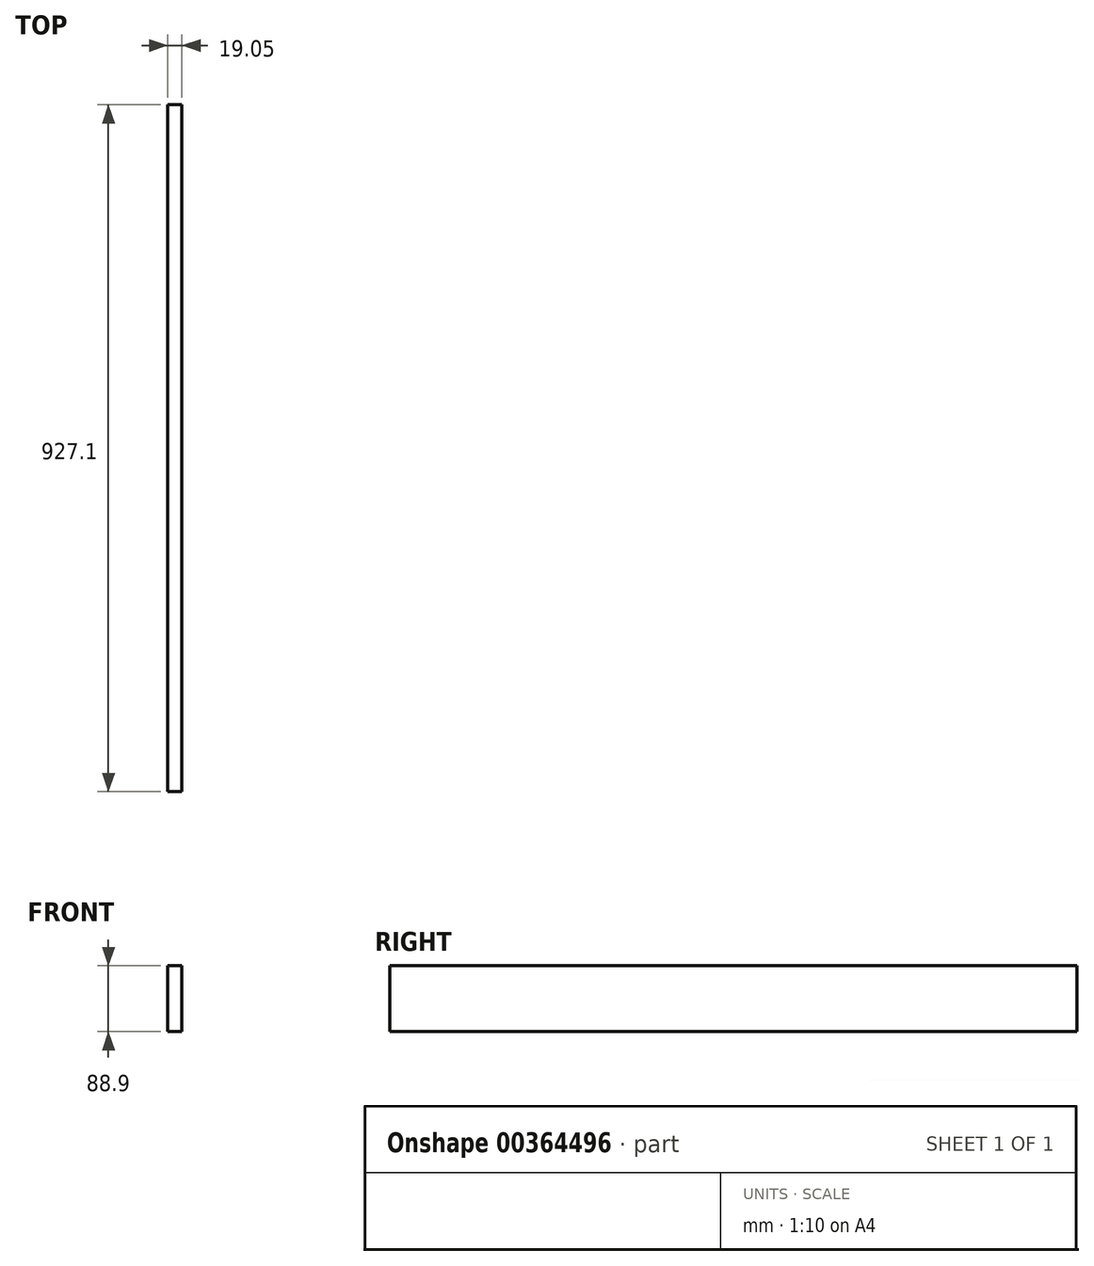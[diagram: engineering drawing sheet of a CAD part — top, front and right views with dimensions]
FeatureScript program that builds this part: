
annotation { "Feature Type Name" : "Feature", "Feature Type Description" : "" }
export const myFeature = defineFeature(function(context is Context, id is Id, definition is map)
    precondition{}
    {
        {
            var Q0;
            Q0=qCreatedBy(makeId("Right.planeOp"),FACE);
            var sketch = newSketch(context, id + "F0", { "sketchPlane" : qUnion([Q0])});
            skLineSegment(sketch, "E0.bottom", {"start": v(0, 0) * mm, "end": v(927.1, 0) * mm});
            skLineSegment(sketch, "E0.top", {"start": v(0, 88.9) * mm, "end": v(927.1, 88.9) * mm});
            skLineSegment(sketch, "E0.left", {"start": v(0, 0) * mm, "end": v(0, 88.9) * mm});
            skLineSegment(sketch, "E0.right", {"start": v(927.1, 0) * mm, "end": v(927.1, 88.9) * mm});
            skSolve(sketch);
        }
        {
            var Q0;
            Q0=makeQuery(id+"F0.imprint","IMPRINT",FACE,{"disambiguationData":[TD([[makeQuery(id+"F0.imprint","IMPRINT",EDGE,{"derivedFrom":sQuery(id+"F0.wireOp",EDGE,"E0.bottom")}),1.0]])]});
            extrude(context, id + "F1", {"entities" : qUnion([Q0]), "depth" : 19.05 * mm});
        }
    });
